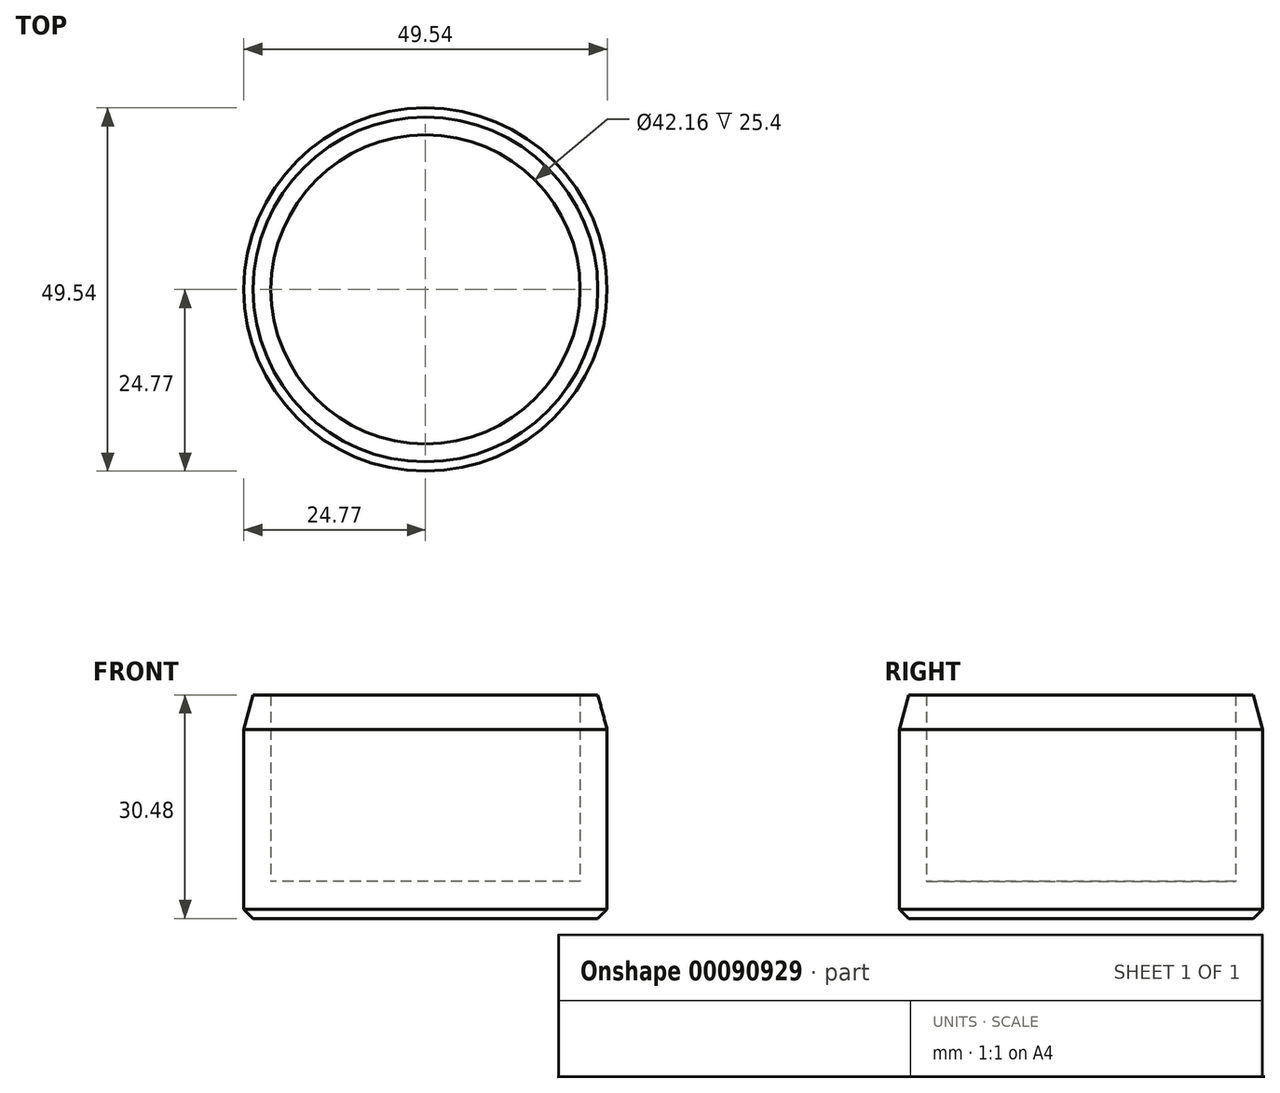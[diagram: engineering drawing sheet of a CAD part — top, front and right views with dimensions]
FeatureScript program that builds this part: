
annotation { "Feature Type Name" : "Feature", "Feature Type Description" : "" }
export const myFeature = defineFeature(function(context is Context, id is Id, definition is map)
    precondition{}
    {
        {
            var Q0;
            Q0=qCreatedBy(makeId("Top.planeOp"),FACE);
            var sketch = newSketch(context, id + "F0", { "sketchPlane" : qUnion([Q0])});
            skCircle(sketch, "E0", {"center": v(0, 0) * mm, "radius": 21.08 * mm});
            skCircle(sketch, "E1", {"center": v(0, 0) * mm, "radius": 24.77 * mm});
            skSolve(sketch);
        }
        {
            var Q0;
            Q0 = qSketchRegion(id + "F0", true);
            extrude(context, id + "F1", {"entities" : qUnion([Q0]), "depth" : 30.48 * mm});
        }
        {
            var Q0;
            Q0=makeQuery(id+"F0.imprint","IMPRINT",FACE,{"disambiguationData":[TD([[makeQuery(id+"F0.imprint","IMPRINT",EDGE,{"derivedFrom":sQuery(id+"F0.wireOp",EDGE,"E0")}),1.0]])]});
            var Q1;
            Q1=makeQuery(id+"F0.imprint","IMPRINT",FACE,{"disambiguationData":[TD([[makeQuery(id+"F0.imprint","IMPRINT",EDGE,{"derivedFrom":sQuery(id+"F0.wireOp",EDGE,"E0")}),-1.0]])]});
            extrude(context, id + "F2", {"entities" : qUnion([Q0, Q1]), "operationType" : NewBodyOperationType.ADD, "depth" : 5.08 * mm});
        }
        {
            var Q0;
            Q0=makeQuery(id+"F1.opExtrude","CAP_EDGE",EDGE,{"disambiguationData":[OSD([sQuery(id+"F0.wireOp",EDGE,"E1")])],"isStart":false});
            chamfer(context, id + "F3", {"entities" : qUnion([Q0]), "chamferType" : ChamferType.OFFSET_ANGLE, "width" : 1.27 * mm, "oppositeDirection" : false, "angle" : 75 * degree, "tangentPropagation" : true});
        }
        {
            var Q0;
            Q0=makeQuery(id+"F1.opExtrude","CAP_EDGE",EDGE,{"disambiguationData":[OSD([sQuery(id+"F0.wireOp",EDGE,"E1")])],"isStart":true});
            chamfer(context, id + "F4", {"entities" : qUnion([Q0]), "width" : 1.27 * mm, "tangentPropagation" : true});
        }
    });
